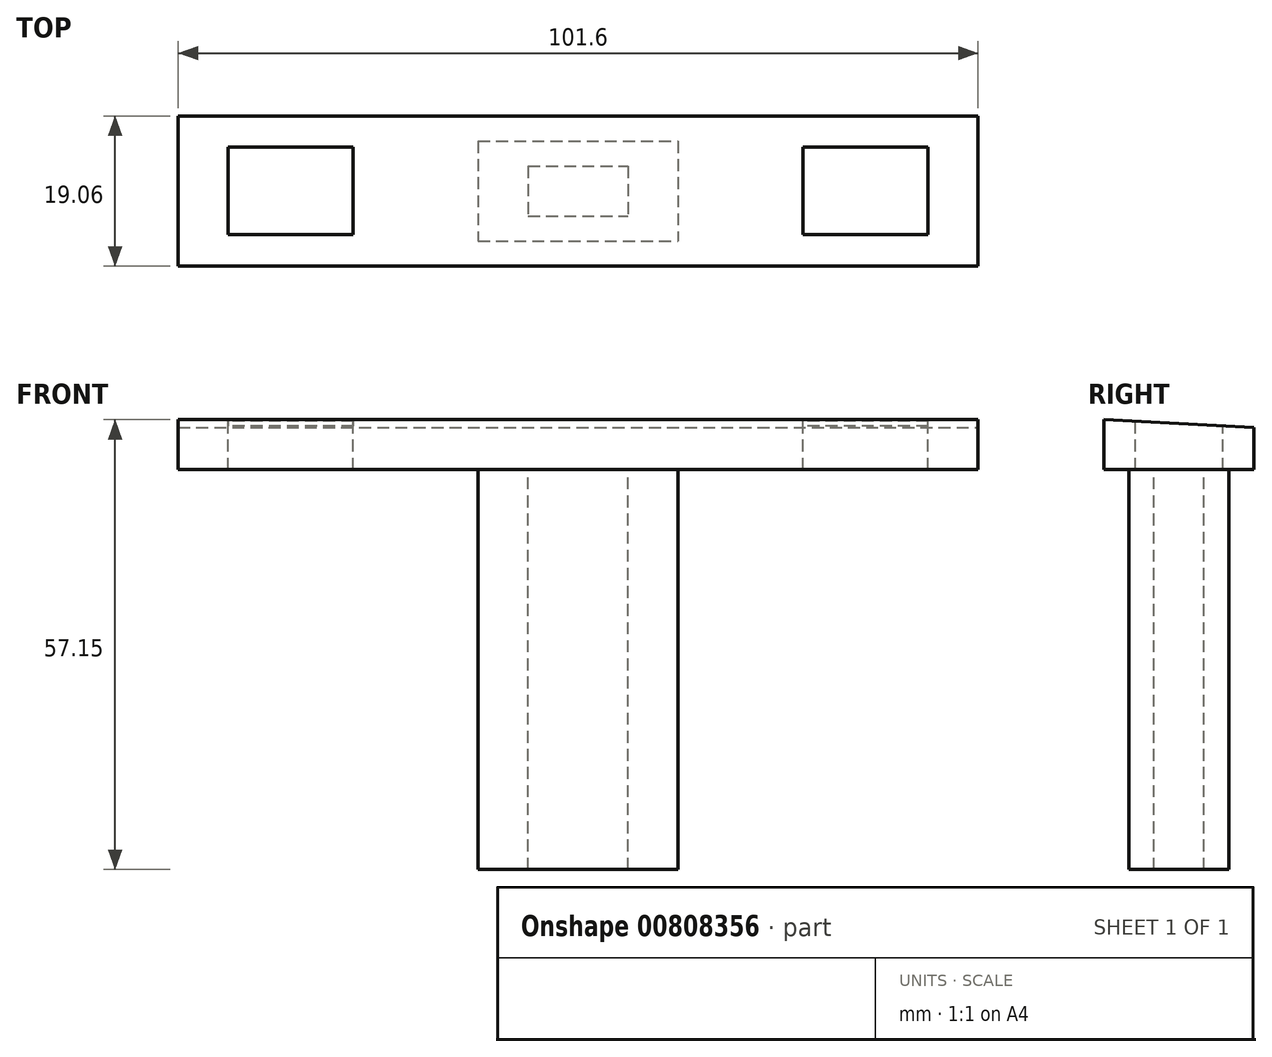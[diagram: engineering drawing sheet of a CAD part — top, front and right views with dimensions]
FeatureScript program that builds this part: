
annotation { "Feature Type Name" : "Feature", "Feature Type Description" : "" }
export const myFeature = defineFeature(function(context is Context, id is Id, definition is map)
    precondition{}
    {
        {
            var Q0;
            Q0=qCreatedBy(makeId("Top.planeOp"),FACE);
            var sketch = newSketch(context, id + "F0", { "sketchPlane" : qUnion([Q0])});
            skLineSegment(sketch, "E0.bottom", {"start": v(50.8, -9.53) * mm, "end": v(-50.8, -9.53) * mm});
            skLineSegment(sketch, "E0.top", {"start": v(50.8, 9.53) * mm, "end": v(-50.8, 9.53) * mm});
            skLineSegment(sketch, "E0.left", {"start": v(50.8, -9.53) * mm, "end": v(50.8, 9.52) * mm});
            skLineSegment(sketch, "E0.right", {"start": v(-50.8, -9.53) * mm, "end": v(-50.8, 9.52) * mm});
            skPoint(sketch, "E0.middle", {"position": v(0, 0) * mm});
            skSolve(sketch);
        }
        {
            var Q0;
            Q0=makeQuery(id+"F0.imprint","IMPRINT",FACE,{"disambiguationData":[TD([[makeQuery(id+"F0.imprint","IMPRINT",EDGE,{"derivedFrom":sQuery(id+"F0.wireOp",EDGE,"E0.bottom")}),-1.0]])]});
            extrude(context, id + "F1", {"entities" : qUnion([Q0]), "depth" : 6.35 * mm, "offsetDistance" : 25.4 * mm});
        }
        {
            var Q0;
            Q0=makeQuery(id+"F1.opExtrude","CAP_FACE",FACE,{"disambiguationData":[OSD([sQuery(id+"F0.wireOp",EDGE,"E0.bottom"),sQuery(id+"F0.wireOp",EDGE,"E0.top"),sQuery(id+"F0.wireOp",EDGE,"E0.left"),sQuery(id+"F0.wireOp",EDGE,"E0.right")])],"isStart":false});
            var sketch = newSketch(context, id + "F2", { "sketchPlane" : qUnion([Q0])});
            skLineSegment(sketch, "E1.bottom", {"start": v(-28.58, -5.56) * mm, "end": v(-44.45, -5.56) * mm});
            skLineSegment(sketch, "E1.top", {"start": v(-28.58, 5.56) * mm, "end": v(-44.45, 5.56) * mm});
            skLineSegment(sketch, "E1.left", {"start": v(-28.58, -5.56) * mm, "end": v(-28.57, 5.56) * mm});
            skLineSegment(sketch, "E1.right", {"start": v(-44.45, -5.56) * mm, "end": v(-44.45, 5.56) * mm});
            skPoint(sketch, "E1.middle", {"position": v(-36.51, 0) * mm});
            skSolve(sketch);
        }
        {
            var Q0;
            Q0=makeQuery(id+"F2.imprint","IMPRINT",FACE,{"disambiguationData":[TD([[makeQuery(id+"F2.imprint","IMPRINT",EDGE,{"derivedFrom":sQuery(id+"F2.wireOp",EDGE,"E1.bottom")}),-1.0]])]});
            extrude(context, id + "F3", {"entities" : qUnion([Q0]), "operationType" : NewBodyOperationType.REMOVE, "oppositeDirection" : true, "depth" : 6.35 * mm, "offsetDistance" : 25.4 * mm});
        }
        {
            var Q0;
            Q0=makeQuery(id+"F1.opExtrude","CAP_FACE",FACE,{"disambiguationData":[OSD([sQuery(id+"F0.wireOp",EDGE,"E0.bottom"),sQuery(id+"F0.wireOp",EDGE,"E0.top"),sQuery(id+"F0.wireOp",EDGE,"E0.left"),sQuery(id+"F0.wireOp",EDGE,"E0.right")])],"isStart":false});
            var sketch = newSketch(context, id + "F4", { "sketchPlane" : qUnion([Q0])});
            skLineSegment(sketch, "E2.bottom", {"start": v(44.45, 5.56) * mm, "end": v(28.58, 5.56) * mm});
            skLineSegment(sketch, "E2.top", {"start": v(44.45, -5.56) * mm, "end": v(28.58, -5.56) * mm});
            skLineSegment(sketch, "E2.left", {"start": v(44.45, 5.56) * mm, "end": v(44.45, -5.56) * mm});
            skLineSegment(sketch, "E2.right", {"start": v(28.58, 5.56) * mm, "end": v(28.58, -5.56) * mm});
            skPoint(sketch, "E2.middle", {"position": v(36.51, 0) * mm});
            skSolve(sketch);
        }
        {
            var Q0;
            Q0=makeQuery(id+"F4.imprint","IMPRINT",FACE,{"disambiguationData":[TD([[makeQuery(id+"F4.imprint","IMPRINT",EDGE,{"derivedFrom":sQuery(id+"F4.wireOp",EDGE,"E2.bottom")}),1.0]])]});
            extrude(context, id + "F5", {"entities" : qUnion([Q0]), "operationType" : NewBodyOperationType.REMOVE, "oppositeDirection" : true, "depth" : 6.35 * mm, "offsetDistance" : 25.4 * mm});
        }
        {
            var Q0;
            Q0=makeQuery(id+"F1.opExtrude","SWEPT_FACE",FACE,{"disambiguationData":[OSD([sQuery(id+"F0.wireOp",EDGE,"E0.left")])]});
            var sketch = newSketch(context, id + "F6", { "sketchPlane" : qUnion([Q0])});
            skLineSegment(sketch, "E3", {"start": v(-9.53, 6.35) * mm, "end": v(9.52, 5.35) * mm});
            skLineSegment(sketch, "E4", {"start": v(9.52, 5.35) * mm, "end": v(9.52, 6.35) * mm});
            skLineSegment(sketch, "E5", {"start": v(9.52, 6.35) * mm, "end": v(-9.53, 6.35) * mm});
            skSolve(sketch);
        }
        {
            var Q0;
            Q0 = qSketchRegion(id + "F6", true);
            extrude(context, id + "F7", {"entities" : qUnion([Q0]), "operationType" : NewBodyOperationType.REMOVE, "oppositeDirection" : true, "depth" : 101.6 * mm, "offsetDistance" : 25.4 * mm});
        }
        {
            var Q0;
            Q0=makeQuery(id+"F1.opExtrude","CAP_FACE",FACE,{"disambiguationData":[OSD([sQuery(id+"F0.wireOp",EDGE,"E0.bottom"),sQuery(id+"F0.wireOp",EDGE,"E0.top"),sQuery(id+"F0.wireOp",EDGE,"E0.left"),sQuery(id+"F0.wireOp",EDGE,"E0.right")])],"isStart":true});
            var sketch = newSketch(context, id + "F8", { "sketchPlane" : qUnion([Q0])});
            skLineSegment(sketch, "E6.bottom", {"start": v(-12.7, -6.35) * mm, "end": v(12.7, -6.35) * mm});
            skLineSegment(sketch, "E6.top", {"start": v(-12.7, 6.35) * mm, "end": v(12.7, 6.35) * mm});
            skLineSegment(sketch, "E6.left", {"start": v(-12.7, -6.35) * mm, "end": v(-12.7, 6.35) * mm});
            skLineSegment(sketch, "E6.right", {"start": v(12.7, -6.35) * mm, "end": v(12.7, 6.35) * mm});
            skPoint(sketch, "E6.middle", {"position": v(0, 0) * mm});
            skLineSegment(sketch, "E7.bottom", {"start": v(-6.35, -3.18) * mm, "end": v(6.35, -3.18) * mm});
            skLineSegment(sketch, "E7.top", {"start": v(-6.35, 3.18) * mm, "end": v(6.35, 3.18) * mm});
            skLineSegment(sketch, "E7.left", {"start": v(-6.35, -3.18) * mm, "end": v(-6.35, 3.17) * mm});
            skLineSegment(sketch, "E7.right", {"start": v(6.35, -3.18) * mm, "end": v(6.35, 3.17) * mm});
            skSolve(sketch);
        }
        {
            var Q0;
            Q0 = qSketchRegion(id + "F8", true);
            extrude(context, id + "F9", {"entities" : qUnion([Q0]), "operationType" : NewBodyOperationType.ADD, "depth" : 50.8 * mm, "offsetDistance" : 25.4 * mm});
        }
    });
